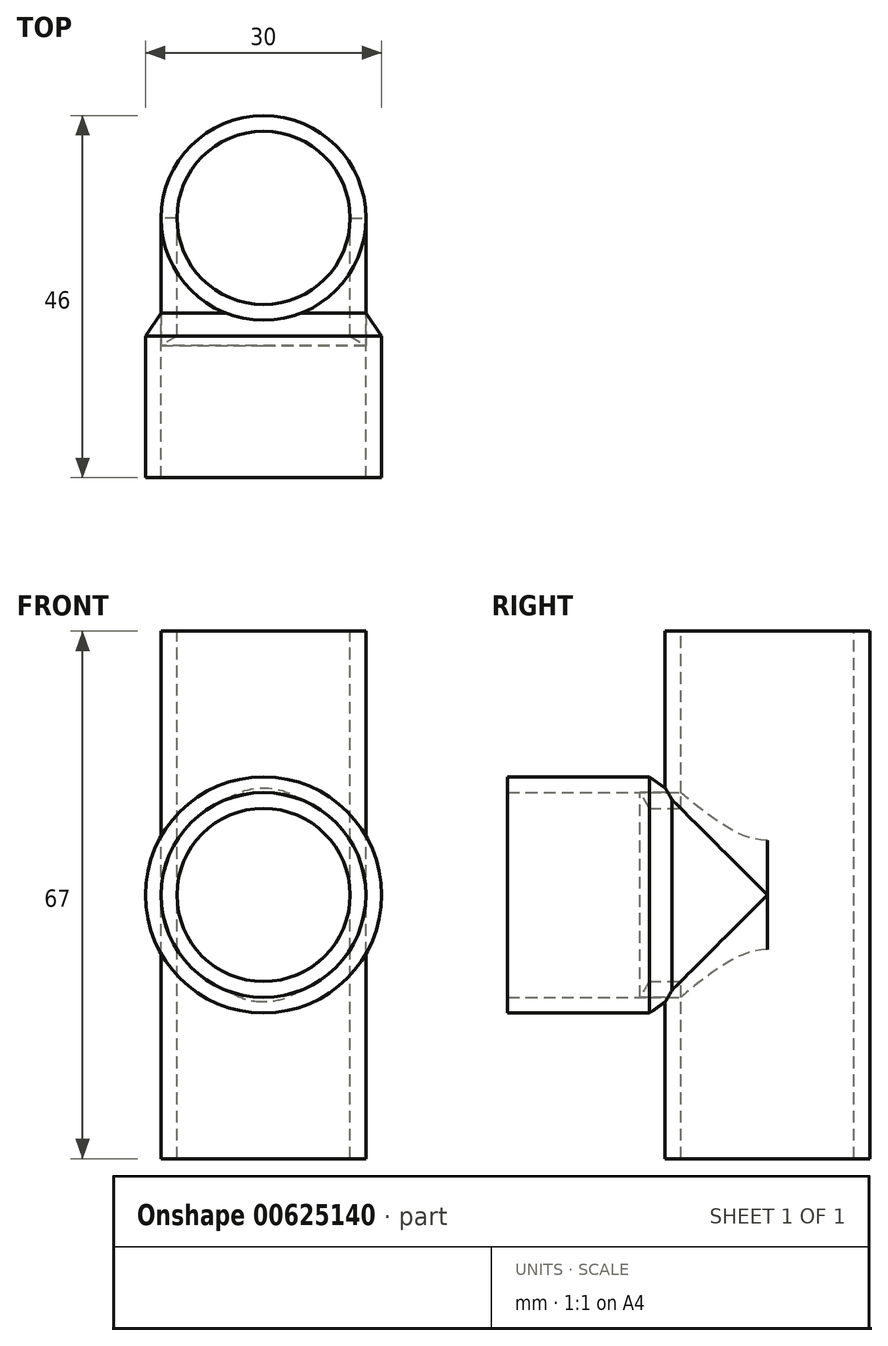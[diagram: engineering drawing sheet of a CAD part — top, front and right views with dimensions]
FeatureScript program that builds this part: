
annotation { "Feature Type Name" : "Feature", "Feature Type Description" : "" }
export const myFeature = defineFeature(function(context is Context, id is Id, definition is map)
    precondition{}
    {
        {
            var Q0;
            Q0=qCreatedBy(makeId("Top.planeOp"),FACE);
            var sketch = newSketch(context, id + "F0", { "sketchPlane" : qUnion([Q0])});
            skCircle(sketch, "E0", {"center": v(0, 0) * mm, "radius": 13 * mm});
            skCircle(sketch, "E1.0", {"center": v(0, 0) * mm, "radius": 11 * mm});
            skSolve(sketch);
        }
        {
            var Q0;
            Q0 = qSketchRegion(id + "F0", true);
            extrude(context, id + "F1", {"entities" : qUnion([Q0]), "oppositeDirection" : true, "depth" : 33.5 * mm, "offsetDistance" : 25 * mm});
        }
        {
            var Q0;
            Q0=qCreatedBy(makeId("Front.planeOp"),FACE);
            var sketch = newSketch(context, id + "F2", { "sketchPlane" : qUnion([Q0])});
            skCircle(sketch, "E2", {"center": v(0, 0) * mm, "radius": 13 * mm});
            skSolve(sketch);
        }
        {
            var Q0;
            Q0 = qSketchRegion(id + "F2", true);
            extrude(context, id + "F3", {"entities" : qUnion([Q0]), "operationType" : NewBodyOperationType.REMOVE, "depth" : 25 * mm, "offsetDistance" : 25 * mm});
        }
        {
            var Q0;
            Q0=makeQuery(id+"F1.opExtrude","SWEPT_BODY",BODY,{"disambiguationData":[OSD([sQuery(id+"F0.wireOp",EDGE,"E0"),sQuery(id+"F0.wireOp",EDGE,"E1.0")])]});
            var Q1;
            Q1=qCreatedBy(makeId("Top.planeOp"),FACE);
            mirror(context, id + "F4", {"operationType" : NewBodyOperationType.ADD, "entities" : qUnion([Q0]), "mirrorPlane" : qUnion([Q1])});
        }
        {
            var Q0;
            Q0=qCreatedBy(makeId("Front.planeOp"),FACE);
            var sketch = newSketch(context, id + "F5", { "sketchPlane" : qUnion([Q0])});
            skCircle(sketch, "E3", {"center": v(0, 0) * mm, "radius": 13 * mm});
            skCircle(sketch, "E4.0", {"center": v(0, 0) * mm, "radius": 11 * mm});
            skSolve(sketch);
        }
        {
            var Q0;
            Q0 = qSketchRegion(id + "F5", true);
            extrude(context, id + "F6", {"entities" : qUnion([Q0]), "depth" : 15 * mm, "offsetDistance" : 25 * mm});
        }
        {
            var Q0;
            Q0=qCreatedBy(makeId("Top.planeOp"),FACE);
            var sketch = newSketch(context, id + "F7", { "sketchPlane" : qUnion([Q0])});
            skCircle(sketch, "E5", {"center": v(0, 0) * mm, "radius": 11 * mm});
            skSolve(sketch);
        }
        {
            var Q0;
            Q0 = qSketchRegion(id + "F7", true);
            extrude(context, id + "F8", {"entities" : qUnion([Q0]), "operationType" : NewBodyOperationType.REMOVE, "endBound" : BoundingType.SYMMETRIC, "oppositeDirection" : true, "depth" : 70 * mm, "offsetDistance" : 25 * mm});
        }
        {
            var Q0;
            Q0=qCreatedBy(makeId("Right.planeOp"),FACE);
            var sketch = newSketch(context, id + "F9", { "sketchPlane" : qUnion([Q0])});
            skLineSegment(sketch, "E6", {"start": v(-15, 13) * mm, "end": v(-12.1, 13) * mm});
            skLineSegment(sketch, "E7", {"start": v(-12.1, 13) * mm, "end": v(-15, 15) * mm});
            skLineSegment(sketch, "E8", {"start": v(-15, 15) * mm, "end": v(-15, 13) * mm});
            skSolve(sketch);
        }
        {
            var Q0;
            Q0 = qSketchRegion(id + "F9", true);
            var Q1;
            Q1=makeQuery(id+"F6.opExtrude","SWEPT_FACE",FACE,{"disambiguationData":[OSD([sQuery(id+"F5.wireOp",EDGE,"E3")])]});
            revolve(context, id + "F10", {"operationType" : NewBodyOperationType.ADD, "entities" : qUnion([Q0]), "axis" : qUnion([Q1]), "revolveType" : RevolveType.FULL});
        }
        {
            var Q0;
            Q0=makeQuery(id+"F6.opExtrude","CAP_FACE",FACE,{"disambiguationData":[OSD([sQuery(id+"F5.wireOp",EDGE,"E3"),sQuery(id+"F5.wireOp",EDGE,"E4.0")])],"isStart":false});
            var sketch = newSketch(context, id + "F11", { "sketchPlane" : qUnion([Q0])});
            skCircle(sketch, "E9", {"center": v(0, 0) * mm, "radius": 15 * mm});
            skCircle(sketch, "E10.0", {"center": v(0, 0) * mm, "radius": 13 * mm});
            skSolve(sketch);
        }
        {
            var Q0;
            Q0 = qSketchRegion(id + "F11", true);
            extrude(context, id + "F12", {"entities" : qUnion([Q0]), "operationType" : NewBodyOperationType.ADD, "depth" : 18 * mm, "offsetDistance" : 25 * mm});
        }
        {
            var Q0;
            Q0=qCreatedBy(makeId("Top.planeOp"),FACE);
            var sketch = newSketch(context, id + "F13", { "sketchPlane" : qUnion([Q0])});
            skLineSegment(sketch, "E11", {"start": v(-13, -15) * mm, "end": v(-11, -15) * mm});
            skLineSegment(sketch, "E12", {"start": v(-13, -15) * mm, "end": v(-13, -16.19) * mm});
            skLineSegment(sketch, "E13", {"start": v(-13, -16.19) * mm, "end": v(-11, -15) * mm});
            skSolve(sketch);
        }
        {
            var Q0;
            Q0 = qSketchRegion(id + "F13", true);
            var Q1;
            Q1=makeQuery(id+"F12.opExtrude","SWEPT_FACE",FACE,{"disambiguationData":[OSD([sQuery(id+"F11.wireOp",EDGE,"E9")])]});
            revolve(context, id + "F14", {"operationType" : NewBodyOperationType.ADD, "entities" : qUnion([Q0]), "axis" : qUnion([Q1]), "revolveType" : RevolveType.FULL});
        }
    });
